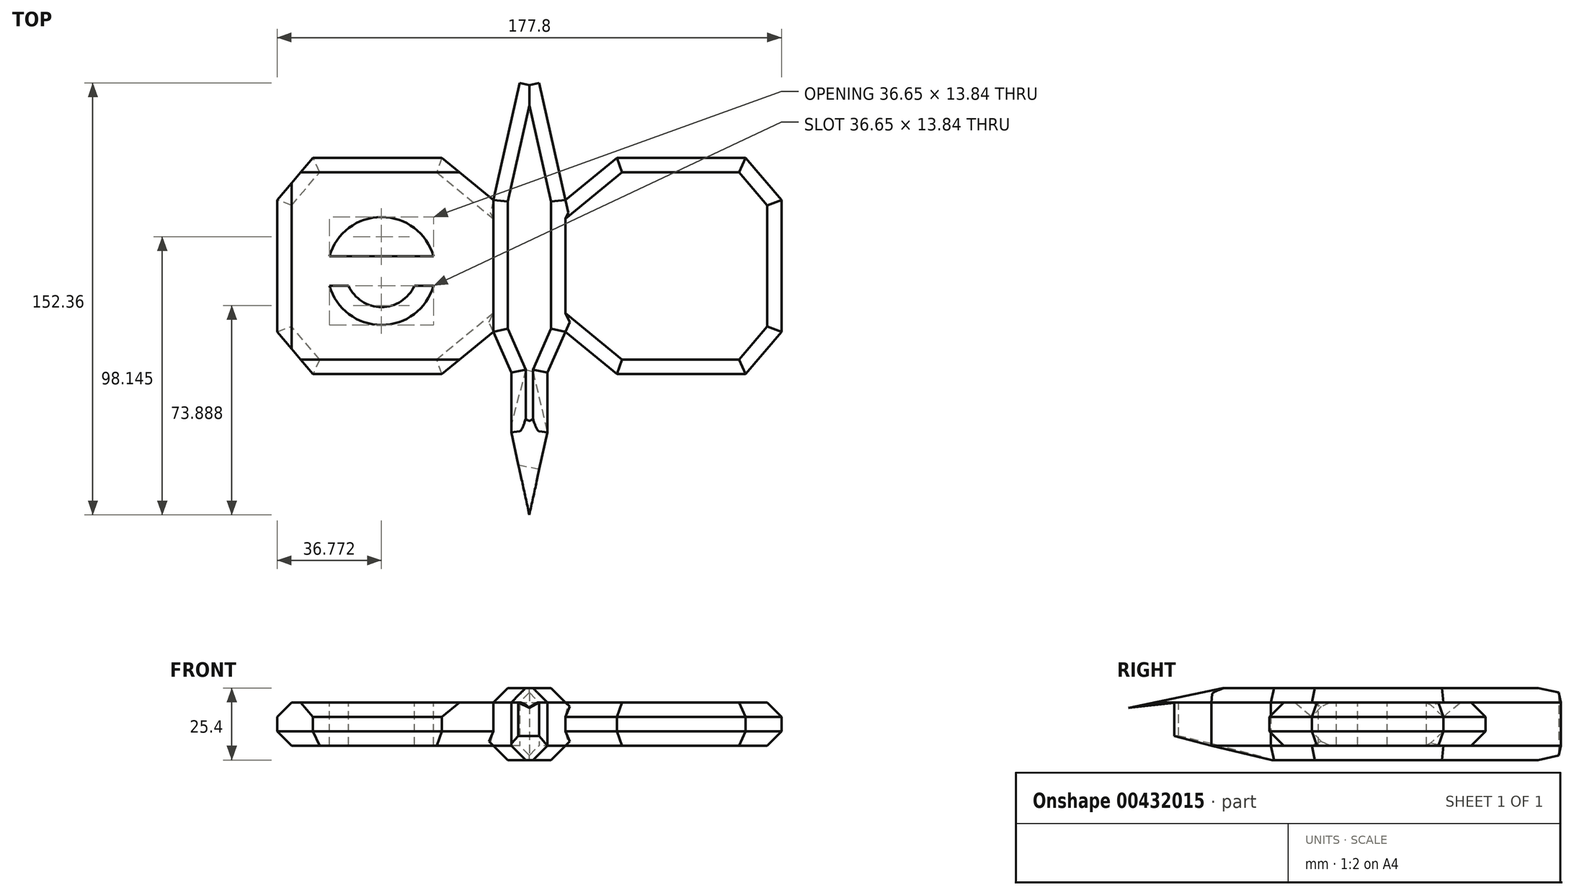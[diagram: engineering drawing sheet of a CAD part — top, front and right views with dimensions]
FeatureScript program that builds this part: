
annotation { "Feature Type Name" : "Feature", "Feature Type Description" : "" }
export const myFeature = defineFeature(function(context is Context, id is Id, definition is map)
    precondition{}
    {
        {
            var Q0;
            Q0=qCreatedBy(makeId("Top.planeOp"),FACE);
            var sketch = newSketch(context, id + "F0", { "sketchPlane" : qUnion([Q0])});
            skLineSegment(sketch, "E0", {"start": v(0, -75.69) * mm, "end": v(6.35, -46.54) * mm});
            skLineSegment(sketch, "E1", {"start": v(6.35, -46.54) * mm, "end": v(6.35, -25.5) * mm});
            skLineSegment(sketch, "E2", {"start": v(6.35, -25.5) * mm, "end": v(12.7, -11.09) * mm});
            skLineSegment(sketch, "E3", {"start": v(12.7, -11.09) * mm, "end": v(12.7, 35.35) * mm});
            skLineSegment(sketch, "E4", {"start": v(12.7, 35.35) * mm, "end": v(3.41, 76.67) * mm});
            skLineSegment(sketch, "E5", {"start": v(3.41, 76.67) * mm, "end": v(0, 75.9) * mm});
            skLineSegment(sketch, "E6", {"start": v(0, 75.9) * mm, "end": v(0, 0) * mm});
            skLineSegment(sketch, "E7", {"start": v(0, -75.69) * mm, "end": v(0, 0) * mm});
            skLineSegment(sketch, "E8", {"start": v(0, 75.9) * mm, "end": v(0, -75.69) * mm, "construction": true});
            skLineSegment(sketch, "E9", {"start": v(0, 80.35) * mm, "end": v(0, -78.48) * mm, "construction": true});
            skLineSegment(sketch, "E10.MirrorCS", {"start": v(-3.41, 76.67) * mm, "end": v(0, 75.9) * mm});
            skLineSegment(sketch, "E11.MirrorCS", {"start": v(-12.7, 35.35) * mm, "end": v(-3.41, 76.67) * mm});
            skLineSegment(sketch, "E12.MirrorCS", {"start": v(-12.7, -11.09) * mm, "end": v(-12.7, 35.35) * mm});
            skLineSegment(sketch, "E13.MirrorCS", {"start": v(-6.35, -25.5) * mm, "end": v(-12.7, -11.09) * mm});
            skLineSegment(sketch, "E14.MirrorCS", {"start": v(-6.35, -46.54) * mm, "end": v(-6.35, -25.5) * mm});
            skLineSegment(sketch, "E15.MirrorCS", {"start": v(0, -75.69) * mm, "end": v(-6.35, -46.54) * mm});
            skSolve(sketch);
        }
        {
            var Q0;
            Q0=qSketchRegion(id+"F0",true);
            extrude(context, id + "F1", {"entities" : qUnion([Q0]), "depth" : 25.4 * mm});
        }
        {
            var Q0;
            Q0=makeQuery(id+"F1.opExtrude","CAP_EDGE",EDGE,{"disambiguationData":[OSD([sQuery(id+"F0.wireOp",EDGE,"E12.MirrorCS")])],"isStart":false});
            var Q1;
            Q1=makeQuery(id+"F1.opExtrude","CAP_EDGE",EDGE,{"disambiguationData":[OSD([sQuery(id+"F0.wireOp",EDGE,"E3")])],"isStart":false});
            var Q2;
            Q2=makeQuery(id+"F1.opExtrude","CAP_EDGE",EDGE,{"disambiguationData":[OSD([sQuery(id+"F0.wireOp",EDGE,"E12.MirrorCS")])],"isStart":true});
            var Q3;
            Q3=makeQuery(id+"F1.opExtrude","CAP_EDGE",EDGE,{"disambiguationData":[OSD([sQuery(id+"F0.wireOp",EDGE,"E3")])],"isStart":true});
            var Q4;
            Q4=makeQuery(id+"F1.opExtrude","CAP_FACE",FACE,{"disambiguationData":[OSD([sQuery(id+"F0.wireOp",EDGE,"E0"),sQuery(id+"F0.wireOp",EDGE,"E1"),sQuery(id+"F0.wireOp",EDGE,"E2"),sQuery(id+"F0.wireOp",EDGE,"E3"),sQuery(id+"F0.wireOp",EDGE,"E4"),sQuery(id+"F0.wireOp",EDGE,"E5"),sQuery(id+"F0.wireOp",EDGE,"E10.MirrorCS"),sQuery(id+"F0.wireOp",EDGE,"E11.MirrorCS"),sQuery(id+"F0.wireOp",EDGE,"E12.MirrorCS"),sQuery(id+"F0.wireOp",EDGE,"E13.MirrorCS"),sQuery(id+"F0.wireOp",EDGE,"E14.MirrorCS"),sQuery(id+"F0.wireOp",EDGE,"E15.MirrorCS")])],"isStart":true});
            var Q5;
            Q5=makeQuery(id+"F1.opExtrude","CAP_FACE",FACE,{"disambiguationData":[OSD([sQuery(id+"F0.wireOp",EDGE,"E0"),sQuery(id+"F0.wireOp",EDGE,"E1"),sQuery(id+"F0.wireOp",EDGE,"E2"),sQuery(id+"F0.wireOp",EDGE,"E3"),sQuery(id+"F0.wireOp",EDGE,"E4"),sQuery(id+"F0.wireOp",EDGE,"E5"),sQuery(id+"F0.wireOp",EDGE,"E10.MirrorCS"),sQuery(id+"F0.wireOp",EDGE,"E11.MirrorCS"),sQuery(id+"F0.wireOp",EDGE,"E12.MirrorCS"),sQuery(id+"F0.wireOp",EDGE,"E13.MirrorCS"),sQuery(id+"F0.wireOp",EDGE,"E14.MirrorCS"),sQuery(id+"F0.wireOp",EDGE,"E15.MirrorCS")])],"isStart":false});
            chamfer(context, id + "F2", {"entities" : qUnion([Q0, Q1, Q2, Q3, Q4, Q5]), "width" : 5.08 * mm, "tangentPropagation" : true});
        }
        {
            var Q0;
            Q0=makeQuery(id+"F1.opExtrude","SWEPT_FACE",FACE,{"disambiguationData":[OSD([sQuery(id+"F0.wireOp",EDGE,"E12.MirrorCS")])]});
            var sketch = newSketch(context, id + "F3", { "sketchPlane" : qUnion([Q0])});
            skLineSegment(sketch, "E16.bottom", {"start": v(25.97, 20.32) * mm, "end": v(-50.23, 20.32) * mm});
            skLineSegment(sketch, "E16.top", {"start": v(25.97, 5.08) * mm, "end": v(-50.23, 5.08) * mm});
            skLineSegment(sketch, "E16.left", {"start": v(25.97, 20.32) * mm, "end": v(25.97, 5.08) * mm});
            skLineSegment(sketch, "E16.right", {"start": v(-50.23, 20.32) * mm, "end": v(-50.23, 5.08) * mm});
            skPoint(sketch, "E16.middle", {"position": v(-12.13, 12.7) * mm});
            skPoint(sketch, "E16.middle.positionSnap0", {"position": v(11.09, 12.7) * mm});
            skPoint(sketch, "E16.middle.positionSnap1", {"position": v(-12.13, 20.32) * mm});
            skPoint(sketch, "E16.cornerSnap0", {"position": v(-12.13, 20.32) * mm});
            skPoint(sketch, "E16.centerSnap0", {"position": v(11.09, 12.7) * mm});
            skPoint(sketch, "E16.centerSnap1", {"position": v(-12.13, 20.32) * mm});
            skSolve(sketch);
        }
        {
            var Q0;
            Q0=qSketchRegion(id+"F3",true);
            extrude(context, id + "F4", {"entities" : qUnion([Q0]), "operationType" : NewBodyOperationType.ADD, "depth" : 76.2 * mm});
        }
        {
            var Q0;
            Q0=makeQuery(id+"F4.opExtrude","SWEPT_FACE",FACE,{"disambiguationData":[OSD([sQuery(id+"F3.wireOp",EDGE,"E16.bottom")])]});
            var sketch = newSketch(context, id + "F5", { "sketchPlane" : qUnion([Q0])});
            skLineSegment(sketch, "E17", {"start": v(-30.86, 50.23) * mm, "end": v(-12.7, 35.35) * mm});
            skLineSegment(sketch, "E18", {"start": v(-12.7, 35.35) * mm, "end": v(-12.7, -11.09) * mm});
            skLineSegment(sketch, "E19", {"start": v(-12.7, -11.09) * mm, "end": v(-30.86, -25.97) * mm});
            skLineSegment(sketch, "E20", {"start": v(-30.86, -25.97) * mm, "end": v(-76.26, -25.97) * mm});
            skLineSegment(sketch, "E21", {"start": v(-76.26, -25.97) * mm, "end": v(-88.9, -11.09) * mm});
            skLineSegment(sketch, "E22", {"start": v(-88.9, -11.09) * mm, "end": v(-88.9, 35.35) * mm});
            skLineSegment(sketch, "E23", {"start": v(-88.9, 35.35) * mm, "end": v(-76.26, 50.23) * mm});
            skLineSegment(sketch, "E24", {"start": v(-76.26, 50.23) * mm, "end": v(-30.86, 50.23) * mm});
            skLineSegment(sketch, "E25", {"start": v(0, 76.7) * mm, "end": v(0, -76.41) * mm, "construction": true});
            skLineSegment(sketch, "E26.MirrorCS", {"start": v(30.86, 50.23) * mm, "end": v(12.7, 35.35) * mm});
            skLineSegment(sketch, "E27.MirrorCS", {"start": v(76.26, 50.23) * mm, "end": v(30.86, 50.23) * mm});
            skLineSegment(sketch, "E28.MirrorCS", {"start": v(88.9, 35.35) * mm, "end": v(76.26, 50.23) * mm});
            skLineSegment(sketch, "E29.MirrorCS", {"start": v(76.26, -25.97) * mm, "end": v(88.9, -11.09) * mm});
            skLineSegment(sketch, "E30.MirrorCS", {"start": v(12.7, -11.09) * mm, "end": v(30.86, -25.97) * mm});
            skLineSegment(sketch, "E31.MirrorCS", {"start": v(12.7, 35.35) * mm, "end": v(12.7, -11.09) * mm});
            skLineSegment(sketch, "E32.MirrorCS", {"start": v(88.9, -11.09) * mm, "end": v(88.9, 35.35) * mm});
            skLineSegment(sketch, "E33.MirrorCS", {"start": v(30.86, -25.97) * mm, "end": v(76.26, -25.97) * mm});
            skSolve(sketch);
        }
        {
            var Q0;
            {var subQ0=sQuery(id+"F5.wireOp",EDGE,"E23");Q0=makeQuery(id+"F5.imprint","IMPRINT",FACE,{"disambiguationData":[TD([[makeQuery(id+"F5.imprint","IMPRINT",EDGE,{"derivedFrom":subQ0}),1.0]])]});}
            var Q1;
            {var subQ0=sQuery(id+"F5.wireOp",EDGE,"E17");Q1=makeQuery(id+"F5.imprint","IMPRINT",FACE,{"disambiguationData":[TD([[makeQuery(id+"F5.imprint","IMPRINT",EDGE,{"derivedFrom":subQ0}),1.0]])]});}
            var Q2;
            {var subQ0=sQuery(id+"F5.wireOp",EDGE,"E19");Q2=makeQuery(id+"F5.imprint","IMPRINT",FACE,{"disambiguationData":[TD([[makeQuery(id+"F5.imprint","IMPRINT",EDGE,{"derivedFrom":subQ0}),1.0]])]});}
            var Q3;
            {var subQ0=sQuery(id+"F5.wireOp",EDGE,"E21");Q3=makeQuery(id+"F5.imprint","IMPRINT",FACE,{"disambiguationData":[TD([[makeQuery(id+"F5.imprint","IMPRINT",EDGE,{"derivedFrom":subQ0}),1.0]])]});}
            extrude(context, id + "F6", {"entities" : qUnion([Q0, Q1, Q2, Q3]), "operationType" : NewBodyOperationType.REMOVE, "oppositeDirection" : true, "depth" : 25.4 * mm});
        }
        {
            var Q0;
            Q0=makeQuery(id+"F1.opExtrude","SWEPT_FACE",FACE,{"disambiguationData":[OSD([sQuery(id+"F0.wireOp",EDGE,"E0")])]});
            var sketch = newSketch(context, id + "F7", { "sketchPlane" : qUnion([Q0])});
            skLineSegment(sketch, "E34", {"start": v(-73.95, 12.7) * mm, "end": v(-44.12, 5.08) * mm});
            skLineSegment(sketch, "E35", {"start": v(-44.12, 5.08) * mm, "end": v(-21.55, -0.68) * mm});
            skLineSegment(sketch, "E36", {"start": v(-21.55, -0.68) * mm, "end": v(-74.55, 0) * mm});
            skLineSegment(sketch, "E37", {"start": v(-74.55, 0) * mm, "end": v(-73.95, 12.7) * mm});
            skSolve(sketch);
        }
        {
            var Q0;
            Q0=qSketchRegion(id+"F7",true);
            extrude(context, id + "F8", {"entities" : qUnion([Q0]), "operationType" : NewBodyOperationType.REMOVE, "oppositeDirection" : true, "depth" : 25.4 * mm});
        }
        {
            var Q0;
            Q0=makeQuery(id+"F2.opChamfer","BLEND_EDGE",EDGE,{"blendedFrom":[makeQuery(id+"F1.opExtrude","CAP_EDGE",EDGE,{"disambiguationData":[OSD([sQuery(id+"F0.wireOp",EDGE,"E0")])],"isStart":false}),makeQuery(id+"F1.opExtrude","CAP_EDGE",EDGE,{"disambiguationData":[OSD([sQuery(id+"F0.wireOp",EDGE,"E15.MirrorCS")])],"isStart":false})],"blendedInto":[]});
            fillet(context, id + "F9", {"entities" : qUnion([Q0]), "radius" : 5.08 * mm, "tangentPropagation" : true, "allowEdgeOverflow" : false});
        }
        {
            var Q0;
            Q0=makeQuery(id+"F1.opExtrude","SWEPT_FACE",FACE,{"disambiguationData":[OSD([sQuery(id+"F0.wireOp",EDGE,"E0")])]});
            var sketch = newSketch(context, id + "F10", { "sketchPlane" : qUnion([Q0])});
            skLineSegment(sketch, "E38", {"start": v(-57.46, 20.32) * mm, "end": v(-57.46, 8.49) * mm});
            skLineSegment(sketch, "E39", {"start": v(-57.46, 8.49) * mm, "end": v(-73.95, 12.7) * mm});
            skLineSegment(sketch, "E40", {"start": v(-73.95, 12.7) * mm, "end": v(-73.95, 18.33) * mm});
            skLineSegment(sketch, "E41", {"start": v(-73.95, 18.33) * mm, "end": v(-57.46, 20.32) * mm});
            skSolve(sketch);
        }
        {
            var Q0;
            Q0=qSketchRegion(id+"F10",true);
            extrude(context, id + "F11", {"entities" : qUnion([Q0]), "operationType" : NewBodyOperationType.REMOVE, "oppositeDirection" : true, "depth" : 25.4 * mm});
        }
        {
            var Q0;
            Q0=makeQuery(id+"F4.opExtrude","SWEPT_EDGE",EDGE,{"disambiguationData":[OSD([sQuery(id+"F3.wireOp",EDGE,"E16.bottom"),sQuery(id+"F3.wireOp",EDGE,"E16.left")])]});
            var Q1;
            Q1=makeQuery(id+"F6.boolean.opBoolean","COPY",EDGE,{"derivedFrom":makeQuery(id+"F6.opExtrude","CAP_EDGE",EDGE,{"disambiguationData":[OSD([sQuery(id+"F5.wireOp",EDGE,"E21")])],"isStart":true})});
            var Q2;
            Q2=makeQuery(id+"F6.boolean.opBoolean","COPY",EDGE,{"derivedFrom":makeQuery(id+"F6.opExtrude","CAP_EDGE",EDGE,{"disambiguationData":[OSD([sQuery(id+"F5.wireOp",EDGE,"E19")])],"isStart":true})});
            var Q3;
            Q3=makeQuery(id+"F6.boolean.opBoolean","COPY",EDGE,{"derivedFrom":makeQuery(id+"F6.opExtrude","CAP_EDGE",EDGE,{"disambiguationData":[OSD([sQuery(id+"F5.wireOp",EDGE,"E17")])],"isStart":true})});
            var Q4;
            Q4=makeQuery(id+"F4.opExtrude","SWEPT_EDGE",EDGE,{"disambiguationData":[OSD([sQuery(id+"F3.wireOp",EDGE,"E16.bottom"),sQuery(id+"F3.wireOp",EDGE,"E16.right")])]});
            var Q5;
            Q5=makeQuery(id+"F6.boolean.opBoolean","COPY",EDGE,{"derivedFrom":makeQuery(id+"F6.opExtrude","CAP_EDGE",EDGE,{"disambiguationData":[OSD([sQuery(id+"F5.wireOp",EDGE,"E23")])],"isStart":true})});
            var Q6;
            Q6=makeQuery(id+"F4.opExtrude","CAP_EDGE",EDGE,{"disambiguationData":[OSD([sQuery(id+"F3.wireOp",EDGE,"E16.bottom")])],"isStart":false});
            var Q7;
            Q7=makeQuery(id+"F4.opExtrude","SWEPT_EDGE",EDGE,{"disambiguationData":[OSD([sQuery(id+"F3.wireOp",EDGE,"E16.top"),sQuery(id+"F3.wireOp",EDGE,"E16.left")])]});
            var Q8;
            Q8=makeQuery(id+"F6.boolean.opBoolean","INTERSECT",EDGE,{"derivedFrom":[makeQuery(id+"F4.opExtrude","SWEPT_FACE",FACE,{"disambiguationData":[OSD([sQuery(id+"F3.wireOp",EDGE,"E16.top")])]}),makeQuery(id+"F6.opExtrude","SWEPT_FACE",FACE,{"disambiguationData":[OSD([sQuery(id+"F5.wireOp",EDGE,"E19")])]})]});
            var Q9;
            Q9=makeQuery(id+"F6.boolean.opBoolean","INTERSECT",EDGE,{"derivedFrom":[makeQuery(id+"F4.opExtrude","SWEPT_FACE",FACE,{"disambiguationData":[OSD([sQuery(id+"F3.wireOp",EDGE,"E16.top")])]}),makeQuery(id+"F6.opExtrude","SWEPT_FACE",FACE,{"disambiguationData":[OSD([sQuery(id+"F5.wireOp",EDGE,"E21")])]})]});
            var Q10;
            Q10=makeQuery(id+"F4.opExtrude","CAP_EDGE",EDGE,{"disambiguationData":[OSD([sQuery(id+"F3.wireOp",EDGE,"E16.top")])],"isStart":false});
            var Q11;
            Q11=makeQuery(id+"F6.boolean.opBoolean","INTERSECT",EDGE,{"derivedFrom":[makeQuery(id+"F4.opExtrude","SWEPT_FACE",FACE,{"disambiguationData":[OSD([sQuery(id+"F3.wireOp",EDGE,"E16.top")])]}),makeQuery(id+"F6.opExtrude","SWEPT_FACE",FACE,{"disambiguationData":[OSD([sQuery(id+"F5.wireOp",EDGE,"E23")])]})]});
            var Q12;
            Q12=makeQuery(id+"F4.opExtrude","SWEPT_EDGE",EDGE,{"disambiguationData":[OSD([sQuery(id+"F3.wireOp",EDGE,"E16.top"),sQuery(id+"F3.wireOp",EDGE,"E16.right")])]});
            var Q13;
            Q13=makeQuery(id+"F6.boolean.opBoolean","INTERSECT",EDGE,{"derivedFrom":[makeQuery(id+"F4.opExtrude","SWEPT_FACE",FACE,{"disambiguationData":[OSD([sQuery(id+"F3.wireOp",EDGE,"E16.top")])]}),makeQuery(id+"F6.opExtrude","SWEPT_FACE",FACE,{"disambiguationData":[OSD([sQuery(id+"F5.wireOp",EDGE,"E17")])]})]});
            chamfer(context, id + "F12", {"entities" : qUnion([Q0, Q1, Q2, Q3, Q4, Q5, Q6, Q7, Q8, Q9, Q10, Q11, Q12, Q13]), "width" : 5.08 * mm, "tangentPropagation" : true});
        }
        {
            var Q0;
            Q0=makeQuery(id+"F5.imprint","IMPRINT",FACE,{"disambiguationData":[TD([[makeQuery(id+"F5.imprint","IMPRINT",EDGE,{"derivedFrom":sQuery(id+"F5.wireOp",EDGE,"E26.MirrorCS")}),1.0]])]});
            extrude(context, id + "F13", {"entities" : qUnion([Q0]), "operationType" : NewBodyOperationType.ADD, "oppositeDirection" : true, "depth" : 15.24 * mm});
        }
        {
            var Q0;
            Q0=makeQuery(id+"F13.opExtrude","CAP_EDGE",EDGE,{"disambiguationData":[OSD([sQuery(id+"F5.wireOp",EDGE,"E33.MirrorCS")])],"isStart":false});
            var Q1;
            Q1=makeQuery(id+"F13.opExtrude","CAP_EDGE",EDGE,{"disambiguationData":[OSD([sQuery(id+"F5.wireOp",EDGE,"E30.MirrorCS")])],"isStart":false});
            var Q2;
            Q2=makeQuery(id+"F13.opExtrude","CAP_EDGE",EDGE,{"disambiguationData":[OSD([sQuery(id+"F5.wireOp",EDGE,"E30.MirrorCS")])],"isStart":true});
            var Q3;
            Q3=makeQuery(id+"F13.opExtrude","CAP_EDGE",EDGE,{"disambiguationData":[OSD([sQuery(id+"F5.wireOp",EDGE,"E33.MirrorCS")])],"isStart":true});
            var Q4;
            Q4=makeQuery(id+"F13.opExtrude","CAP_EDGE",EDGE,{"disambiguationData":[OSD([sQuery(id+"F5.wireOp",EDGE,"E29.MirrorCS")])],"isStart":true});
            var Q5;
            Q5=makeQuery(id+"F13.opExtrude","CAP_EDGE",EDGE,{"disambiguationData":[OSD([sQuery(id+"F5.wireOp",EDGE,"E32.MirrorCS")])],"isStart":true});
            var Q6;
            Q6=makeQuery(id+"F13.opExtrude","CAP_EDGE",EDGE,{"disambiguationData":[OSD([sQuery(id+"F5.wireOp",EDGE,"E29.MirrorCS")])],"isStart":false});
            var Q7;
            Q7=makeQuery(id+"F13.opExtrude","CAP_EDGE",EDGE,{"disambiguationData":[OSD([sQuery(id+"F5.wireOp",EDGE,"E32.MirrorCS")])],"isStart":false});
            var Q8;
            Q8=makeQuery(id+"F13.opExtrude","CAP_EDGE",EDGE,{"disambiguationData":[OSD([sQuery(id+"F5.wireOp",EDGE,"E28.MirrorCS")])],"isStart":false});
            var Q9;
            Q9=makeQuery(id+"F13.opExtrude","CAP_EDGE",EDGE,{"disambiguationData":[OSD([sQuery(id+"F5.wireOp",EDGE,"E27.MirrorCS")])],"isStart":false});
            var Q10;
            Q10=makeQuery(id+"F13.opExtrude","CAP_EDGE",EDGE,{"disambiguationData":[OSD([sQuery(id+"F5.wireOp",EDGE,"E26.MirrorCS")])],"isStart":false});
            var Q11;
            Q11=makeQuery(id+"F13.opExtrude","CAP_EDGE",EDGE,{"disambiguationData":[OSD([sQuery(id+"F5.wireOp",EDGE,"E27.MirrorCS")])],"isStart":true});
            var Q12;
            Q12=makeQuery(id+"F13.opExtrude","CAP_EDGE",EDGE,{"disambiguationData":[OSD([sQuery(id+"F5.wireOp",EDGE,"E28.MirrorCS")])],"isStart":true});
            var Q13;
            Q13=makeQuery(id+"F13.opExtrude","CAP_EDGE",EDGE,{"disambiguationData":[OSD([sQuery(id+"F5.wireOp",EDGE,"E26.MirrorCS")])],"isStart":true});
            chamfer(context, id + "F14", {"entities" : qUnion([Q0, Q1, Q2, Q3, Q4, Q5, Q6, Q7, Q8, Q9, Q10, Q11, Q12, Q13]), "width" : 5.08 * mm, "tangentPropagation" : true});
        }
        {
            var Q0;
            Q0=makeQuery(id+"F5.imprint","IMPRINT",FACE,{"disambiguationData":[TD([[makeQuery(id+"F5.imprint","IMPRINT",EDGE,{"derivedFrom":sQuery(id+"F5.wireOp",EDGE,"E17")}),-1.0]])]});
            var sketch = newSketch(context, id + "F15", { "sketchPlane" : qUnion([Q0])});
            skCircle(sketch, "E42", {"center": v(-52.13, 10.33) * mm, "radius": 19.05 * mm});
            skArc(sketch, "E43", {"start": v(-63.71, 5.12) * mm, "mid": v(-52.13, -2.37) * mm, "end": v(-40.54, 5.12) * mm});
            skLineSegment(sketch, "E44", {"start": v(-33.8, 15.53) * mm, "end": v(-70.45, 15.53) * mm});
            skLineSegment(sketch, "E45", {"start": v(-70.45, 5.12) * mm, "end": v(-33.8, 5.12) * mm});
            skArc(sketch, "E46.trimOffspring", {"start": v(-40.54, 15.53) * mm, "mid": v(-52.13, 23.03) * mm, "end": v(-63.71, 15.53) * mm});
            skLineSegment(sketch, "E47", {"start": v(-63.71, 5.12) * mm, "end": v(-70.45, 5.12) * mm});
            skLineSegment(sketch, "E48", {"start": v(-40.54, 5.12) * mm, "end": v(-33.8, 5.12) * mm});
            skLineSegment(sketch, "E49", {"start": v(-33.8, 15.53) * mm, "end": v(-40.54, 15.53) * mm});
            skLineSegment(sketch, "E50", {"start": v(-63.71, 15.53) * mm, "end": v(-70.45, 15.53) * mm});
            skLineSegment(sketch, "E51", {"start": v(-63.71, 15.53) * mm, "end": v(-40.54, 15.53) * mm});
            skLineSegment(sketch, "E52", {"start": v(-40.54, 5.12) * mm, "end": v(-63.71, 5.12) * mm});
            skLineSegment(sketch, "E53", {"start": v(-40.54, 15.53) * mm, "end": v(-63.71, 15.53) * mm});
            skLineSegment(sketch, "E54", {"start": v(-40.54, 15.53) * mm, "end": v(-33.8, 15.53) * mm});
            skSolve(sketch);
        }
        {
            var Q0;
            Q0=makeQuery(id+"F15.imprint","IMPRINT",FACE,{"disambiguationData":[TD([[makeQuery(id+"F15.imprint","IMPRINT",EDGE,{"derivedFrom":sQuery(id+"F15.wireOp",EDGE,"E46.trimOffspring")}),1.0]])]});
            var Q1;
            Q1=makeQuery(id+"F15.imprint","IMPRINT",FACE,{"disambiguationData":[TD([[makeQuery(id+"F15.imprint","IMPRINT",EDGE,{"derivedFrom":sQuery(id+"F15.wireOp",EDGE,"E46.trimOffspring")}),-1.0]])]});
            var Q2;
            Q2=makeQuery(id+"F15.imprint","IMPRINT",FACE,{"disambiguationData":[TD([[makeQuery(id+"F15.imprint","IMPRINT",EDGE,{"derivedFrom":sQuery(id+"F15.wireOp",EDGE,"E43")}),-1.0]])]});
            extrude(context, id + "F16", {"entities" : qUnion([Q0, Q1, Q2]), "operationType" : NewBodyOperationType.REMOVE, "oppositeDirection" : true, "depth" : 25.4 * mm});
        }
    });
